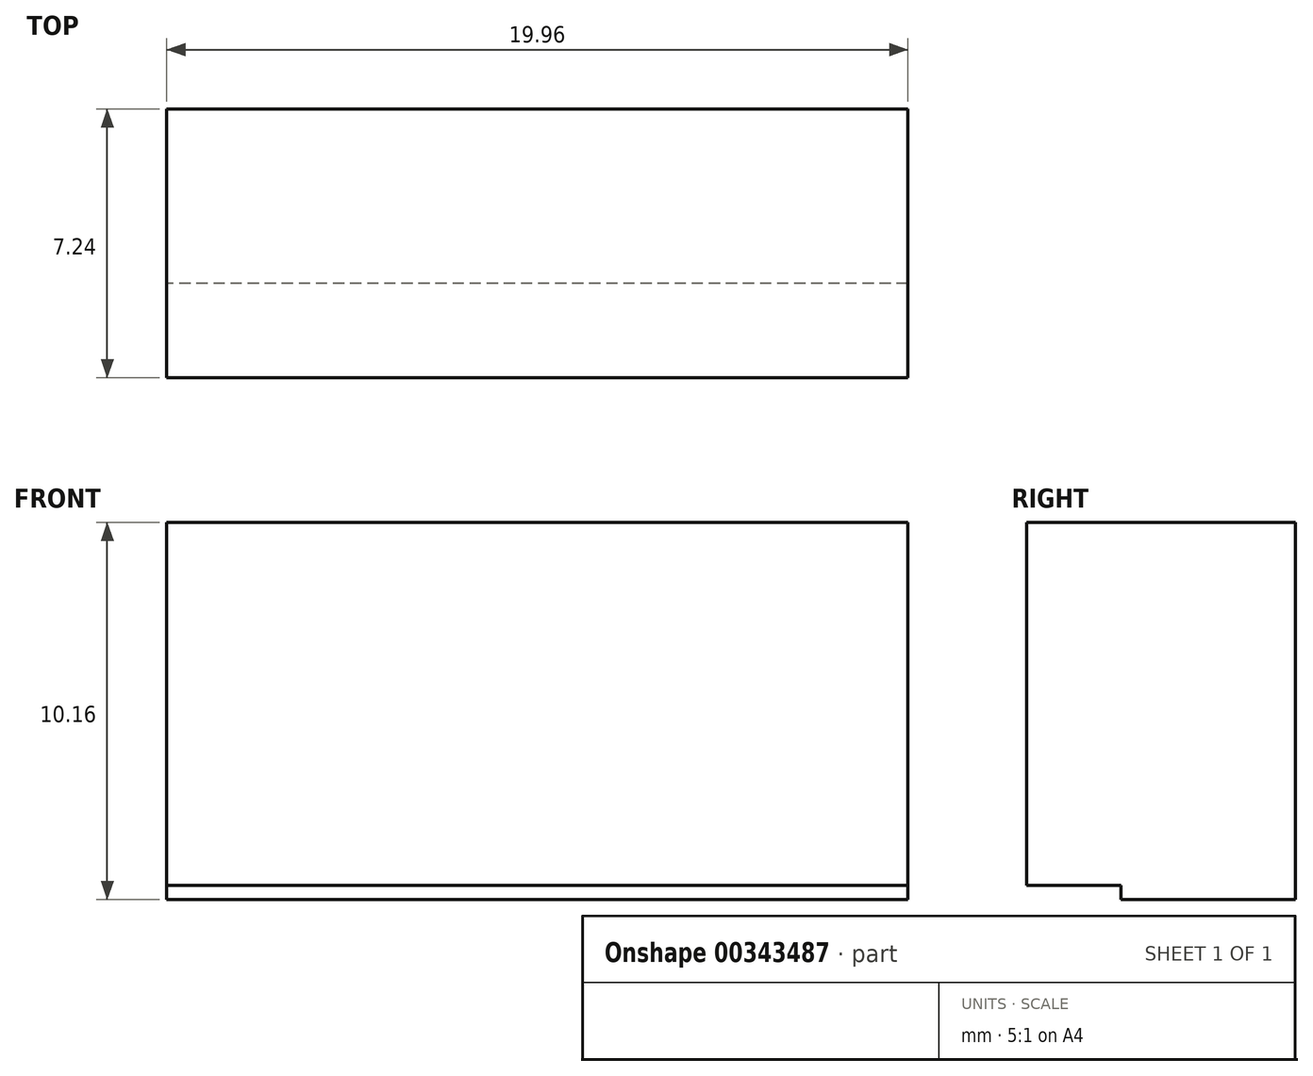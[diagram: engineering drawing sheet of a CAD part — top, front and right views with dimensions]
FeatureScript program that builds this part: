
annotation { "Feature Type Name" : "Feature", "Feature Type Description" : "" }
export const myFeature = defineFeature(function(context is Context, id is Id, definition is map)
    precondition{}
    {
        {
            var Q0;
            Q0=qCreatedBy(makeId("Front.planeOp"),FACE);
            var sketch = newSketch(context, id + "F0", { "sketchPlane" : qUnion([Q0])});
            skLineSegment(sketch, "E0.bottom", {"start": v(9.98, -4.89) * mm, "end": v(-9.98, -4.89) * mm});
            skLineSegment(sketch, "E0.top", {"start": v(9.98, 4.89) * mm, "end": v(-9.98, 4.89) * mm});
            skLineSegment(sketch, "E0.left", {"start": v(9.98, -4.89) * mm, "end": v(9.98, 4.89) * mm});
            skLineSegment(sketch, "E0.right", {"start": v(-9.98, -4.89) * mm, "end": v(-9.98, 4.89) * mm});
            skPoint(sketch, "E0.middle", {"position": v(0, 0) * mm});
            skSolve(sketch);
        }
        {
            var Q0;
            Q0 = qSketchRegion(id + "F0", true);
            extrude(context, id + "F1", {"entities" : qUnion([Q0]), "depth" : 7.24 * mm});
        }
        {
            var Q0;
            Q0=makeQuery(id+"F1.opExtrude","CAP_FACE",FACE,{"disambiguationData":[OSD([sQuery(id+"F0.wireOp",EDGE,"E0.bottom"),sQuery(id+"F0.wireOp",EDGE,"E0.top"),sQuery(id+"F0.wireOp",EDGE,"E0.left"),sQuery(id+"F0.wireOp",EDGE,"E0.right")])],"isStart":true});
            var sketch = newSketch(context, id + "F2", { "sketchPlane" : qUnion([Q0])});
            skLineSegment(sketch, "E1.bottom", {"start": v(-9.98, -4.89) * mm, "end": v(9.98, -4.89) * mm});
            skLineSegment(sketch, "E1.top", {"start": v(-9.98, -5.27) * mm, "end": v(9.98, -5.27) * mm});
            skLineSegment(sketch, "E1.left", {"start": v(-9.98, -4.89) * mm, "end": v(-9.98, -5.27) * mm});
            skLineSegment(sketch, "E1.right", {"start": v(9.98, -4.89) * mm, "end": v(9.98, -5.27) * mm});
            skSolve(sketch);
        }
        {
            var Q0;
            Q0 = qSketchRegion(id + "F2", true);
            extrude(context, id + "F3", {"entities" : qUnion([Q0]), "operationType" : NewBodyOperationType.ADD, "oppositeDirection" : true, "depth" : 4.7 * mm});
        }
    });
